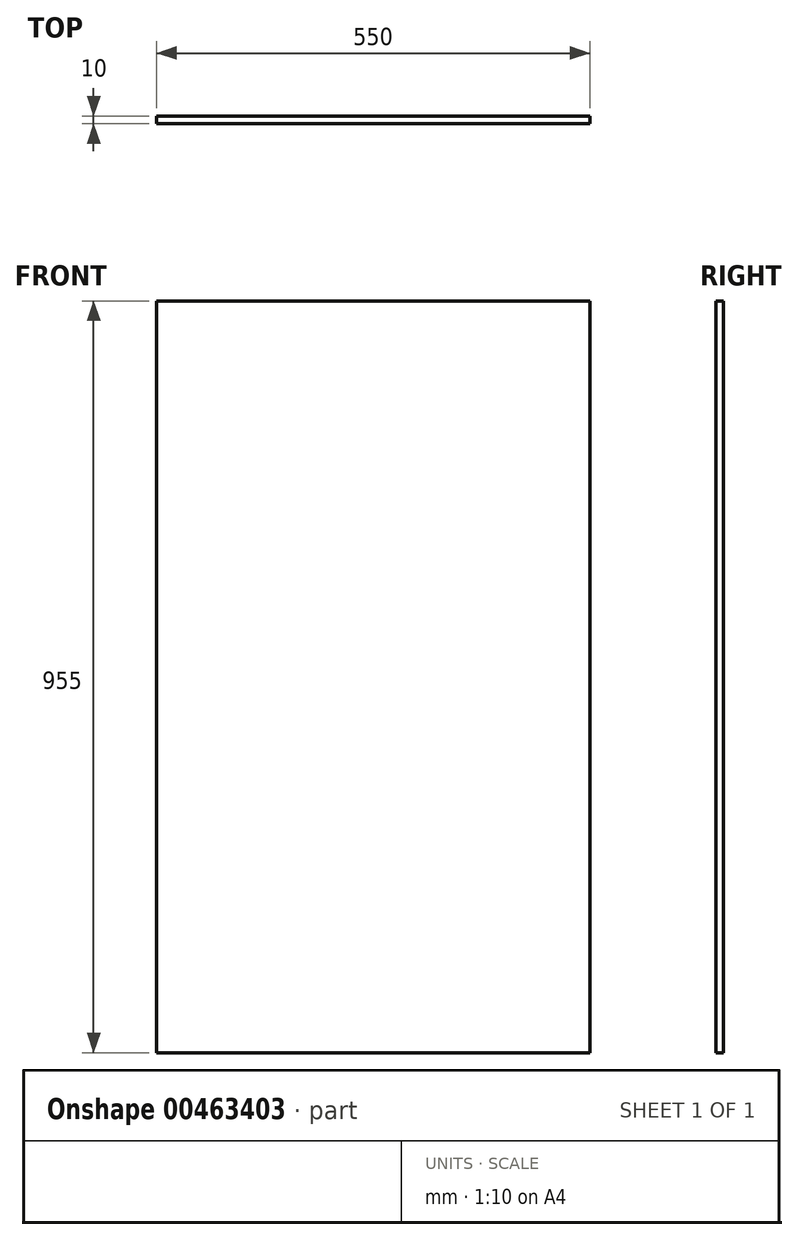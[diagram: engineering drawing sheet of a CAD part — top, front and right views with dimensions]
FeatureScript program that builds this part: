
annotation { "Feature Type Name" : "Feature", "Feature Type Description" : "" }
export const myFeature = defineFeature(function(context is Context, id is Id, definition is map)
    precondition{}
    {
        {
            var Q0;
            Q0=qCreatedBy(makeId("Front.planeOp"),FACE);
            var sketch = newSketch(context, id + "F0", { "sketchPlane" : qUnion([Q0])});
            skLineSegment(sketch, "E0.bottom", {"start": v(0, 0) * mm, "end": v(550, 0) * mm});
            skLineSegment(sketch, "E0.top", {"start": v(0, 955) * mm, "end": v(550, 955) * mm});
            skLineSegment(sketch, "E0.left", {"start": v(0, 0) * mm, "end": v(0, 955) * mm});
            skLineSegment(sketch, "E0.right", {"start": v(550, 0) * mm, "end": v(550, 955) * mm});
            skSolve(sketch);
        }
        {
            var Q0;
            Q0 = qSketchRegion(id + "F0", true);
            extrude(context, id + "F1", {"entities" : qUnion([Q0]), "depth" : 10 * mm});
        }
    });
